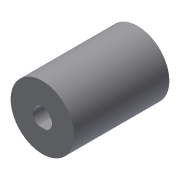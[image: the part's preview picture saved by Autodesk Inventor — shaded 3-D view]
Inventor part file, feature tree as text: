
AUTODESK INVENTOR PART (.ipt)
format: ipt  version: 2019.4 (Build 234330000, 330)  size: 113,152 bytes
history: native  units: mm
features: extrude x3, other x3, sketch x2, reference x1
ambient origin geometry x8: Origin, YZ Plane, XZ Plane, XY Plane, X Axis, Y Axis, Z Axis, Center Point
bodies: Solid1 (feature_tree)
feature tree (9):
  extrude  "Extrusion1"  Depth=10.0mm
  extrude  "Extrusion2"  Depth=10.0mm
  extrude  "Extrusion3"  Depth=5.0mm TaperAngle=0.0deg
  sketch  "Sketch1"  dims[d0=0.1mm d1=10.0mm]
  reference  "Reference1"
  sketch  "Sketch3"  dims[d2=10.0mm d3=0.0mm d4=2.8mm d5=5.0mm d6=0.0mm d7=10.0mm d8=0.0mm d9=60.0deg d10=60.0deg]
  other  "Assembly_Opentrons_Autofocus_v1.iam"
  other  "00_NEMA11:1"
  other  "Welle_11_2"
